# Revit family: P4696-09
name_source: partatom
category: Lighting Fixtures
revit_build: Autodesk Revit 2014 (Build: 20130308_1515(x64)
units: mm (PartAtom-declared; Revit-internal decimal feet)

## types (1)
- P4696-09
    Apparent Load = 100 VA
    Assembly Code = D5020200
    Connector Description = Lighting Connector
    Default Elevation = 48 "
    Description = Invite the beauty of light into your home with this Brushed Nickel five-light chandelier. Invite provides a welcoming silhouette with a unique shade comprised of an inner glass globe encircled by a translucent sheer Mylar shade. The rich, layering effect creates a dreamy look that is both elegant and modern. Offered as a complete collection, the Invite styling can be carried throughout your home or as a focal style in a special room.
    Features = Brushed Nickel finish.
Unique translucent sheer mylar shades.
Inner glass globes provide inviting illumination.
Elegant and dreamy rich, layering effect.
Includes one 6inch, four 12inch stems and 6 links of chain.
    Fixture distribution = Direct
    Glass = Paint - Hubbell - White Texture
    Gold = Hubbell - Gold
    Height = 11 "
    Housing Material = Paint - Hubbell - Light Silver
    Lamp = LED or Medium Base
    Load Classification = Lighting
    Manufacturer = Progress Lighting
    Model = P4696-09
    Power Factor = 1
    Product Documentation Link = https://hubbellcdn.com
    Product Link = https://www.hubbell.com
    Square = 6 "
    URL = https://www.hubbell.com
    Voltage = 120 V
    Warranty = 1 year Warranty
    Wattage Comments = 100W
    Watts = 100 W

## geometry (parser evidence)
native form markers: Sweep x4
no freeform markers — native parametric forms only
